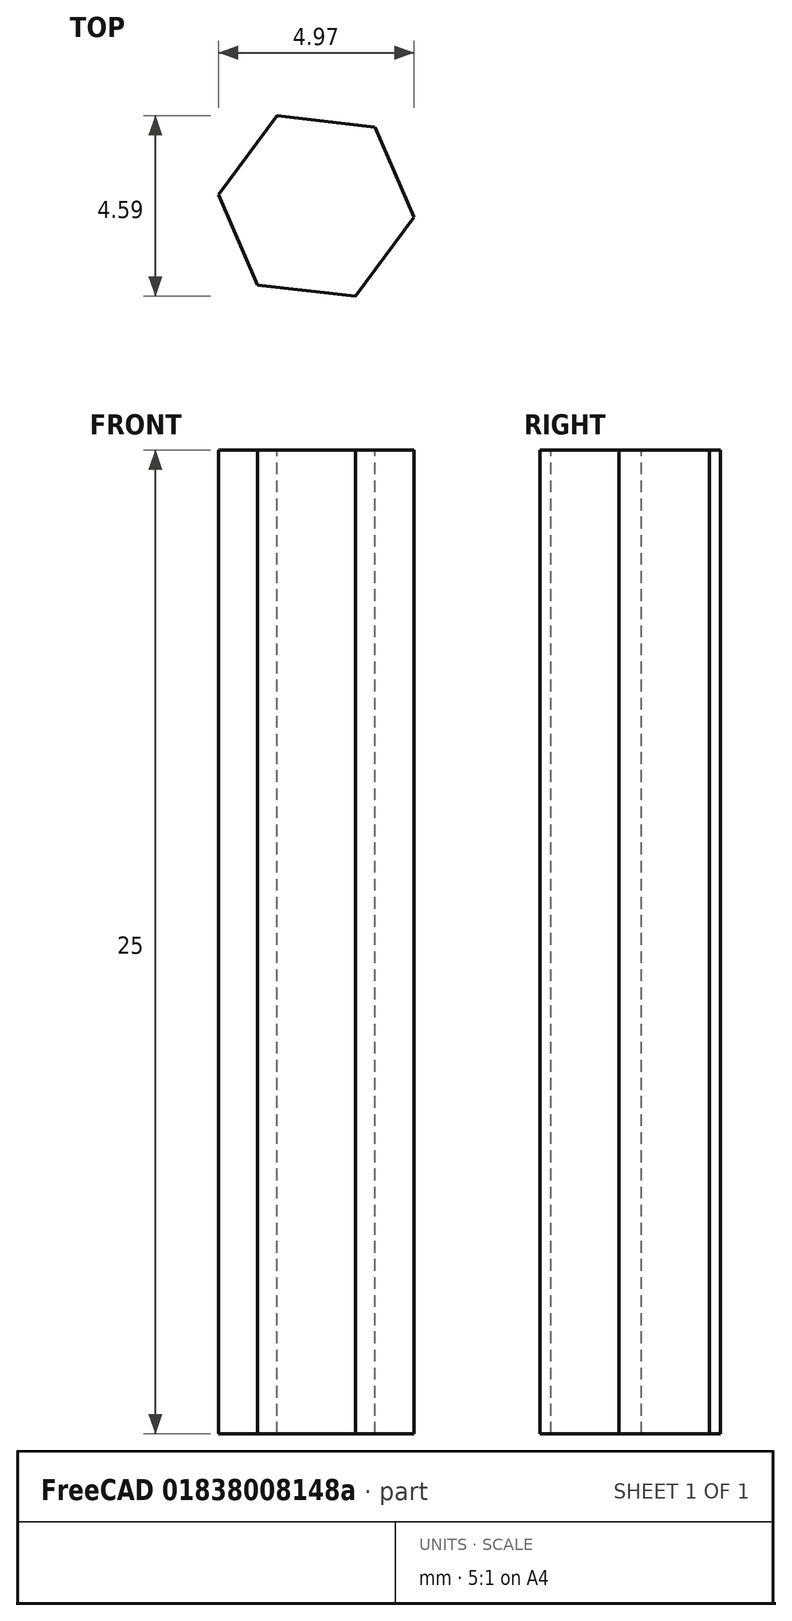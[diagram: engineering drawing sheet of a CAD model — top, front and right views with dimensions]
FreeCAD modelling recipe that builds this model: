
FCSTD DOCUMENT  (FreeCAD 0.16R6704 (Git))
Label: separadores robot
License: All rights reserved
LicenseURL: http://en.wikipedia.org/wiki/All_rights_reserved
objects: Sketcher::SketchObject×1, PartDesign::Pad×1
note: 3 computed .brp shape members not serialized (recipe doc carries the construction recipe); baked Part::Feature solids carry a one-line shape summary decoded from their .brp

FEATURE [Sketcher::SketchObject] Sketch
  sketch-geometry (7):
    g0: LineSegment StartX=-67.9296 StartY=0 StartZ=0 EndX=-66.4401 EndY=2.00781 EndZ=0
    g1: LineSegment StartX=-66.4401 StartY=2.00781 StartZ=0 EndX=-67.4342 EndY=4.30169 EndZ=0
    g2: LineSegment StartX=-67.4342 StartY=4.30169 StartZ=0 EndX=-69.9177 EndY=4.58774 EndZ=0
    g3: LineSegment StartX=-69.9177 StartY=4.58774 StartZ=0 EndX=-71.4073 EndY=2.57993 EndZ=0
    g4: LineSegment StartX=-71.4073 StartY=2.57993 StartZ=0 EndX=-70.4132 EndY=0.286058 EndZ=0
    g5: LineSegment StartX=-70.4132 StartY=0.286058 StartZ=0 EndX=-67.9296 EndY=0 EndZ=0
    g6: Circle [constr] CenterX=-68.9237 CenterY=2.29387 CenterZ=0 NormalX=0 NormalY=0 NormalZ=1 Radius=2.5
  constraints (15):
    c: Coincident(g0,g1)
    c: Coincident(g1,g2)
    c: Coincident(g2,g3)
    c: Coincident(g3,g4)
    c: Coincident(g4,g5)
    c: Coincident(g5,g0)
    c: Equal(g0, g1-g5) x5
    c: PointOnObject(g0,g6)
    c: PointOnObject(g1,g6)
    c: PointOnObject(g2,g6)
    c: PointOnObject(g3,g6)
    c: PointOnObject(g4,g6)
    c: PointOnObject(g5,g6)
    c: PointOnObject(g5,g-1)
    c: Radius(g6) = 2.5
FEATURE [PartDesign::Pad] Pad
  Length = 25
  Length2 = 100
  Sketch = -> Sketch
  Type = 0
